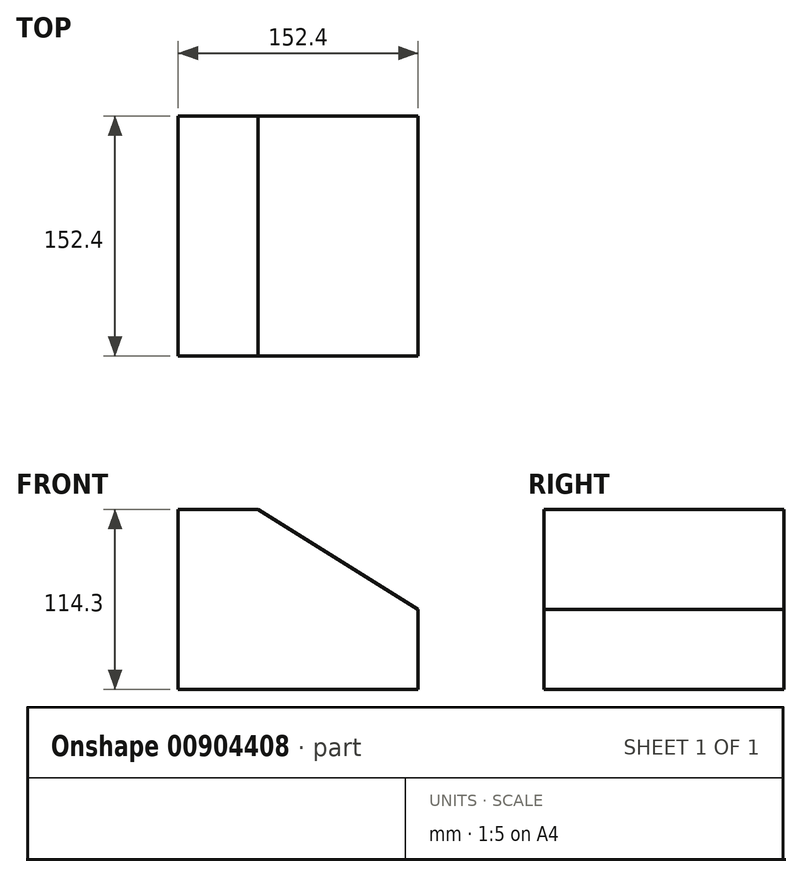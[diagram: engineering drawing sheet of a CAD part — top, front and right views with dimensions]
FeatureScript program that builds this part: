
annotation { "Feature Type Name" : "Feature", "Feature Type Description" : "" }
export const myFeature = defineFeature(function(context is Context, id is Id, definition is map)
    precondition{}
    {
        {
            var Q0;
            Q0=qCreatedBy(makeId("Front.planeOp"),FACE);
            var sketch = newSketch(context, id + "F0", { "sketchPlane" : qUnion([Q0])});
            skLineSegment(sketch, "E0.bottom", {"start": v(-76.2, 57.15) * mm, "end": v(76.2, 57.15) * mm});
            skLineSegment(sketch, "E0.top", {"start": v(-76.2, -57.15) * mm, "end": v(76.2, -57.15) * mm});
            skLineSegment(sketch, "E0.left", {"start": v(-76.2, 57.15) * mm, "end": v(-76.2, -57.15) * mm});
            skLineSegment(sketch, "E0.right", {"start": v(76.2, 57.15) * mm, "end": v(76.2, -57.15) * mm});
            skPoint(sketch, "E0.middle", {"position": v(0, 0) * mm});
            skSolve(sketch);
        }
        {
            var Q0;
            Q0=makeQuery(id+"F0.imprint","IMPRINT",FACE,{"disambiguationData":[TD([[makeQuery(id+"F0.imprint","IMPRINT",EDGE,{"derivedFrom":sQuery(id+"F0.wireOp",EDGE,"E0.bottom")}),-1.0]])]});
            extrude(context, id + "F1", {"entities" : qUnion([Q0]), "depth" : 152.4 * mm, "offsetDistance" : 25.4 * mm});
        }
        {
            var Q0;
            Q0=makeQuery(id+"F1.opExtrude","CAP_FACE",FACE,{"disambiguationData":[OSD([sQuery(id+"F0.wireOp",EDGE,"E0.bottom"),sQuery(id+"F0.wireOp",EDGE,"E0.top"),sQuery(id+"F0.wireOp",EDGE,"E0.left"),sQuery(id+"F0.wireOp",EDGE,"E0.right")])],"isStart":false});
            var sketch = newSketch(context, id + "F2", { "sketchPlane" : qUnion([Q0])});
            skLineSegment(sketch, "E1", {"start": v(-76.2, 57.15) * mm, "end": v(-25.4, 57.15) * mm});
            skLineSegment(sketch, "E2", {"start": v(-25.4, 57.15) * mm, "end": v(76.2, -6.35) * mm});
            skLineSegment(sketch, "E3", {"start": v(76.2, -6.35) * mm, "end": v(76.2, -57.15) * mm});
            skSolve(sketch);
        }
        {
            var Q0;
            {var subQ0=sQuery(id+"F2.wireOp",EDGE,"E2");Q0=makeQuery(id+"F2.imprint","IMPRINT",FACE,{"disambiguationData":[TD([[makeQuery(id+"F2.imprint","IMPRINT",EDGE,{"derivedFrom":subQ0}),1.0]])]});}
            extrude(context, id + "F3", {"entities" : qUnion([Q0]), "operationType" : NewBodyOperationType.REMOVE, "endBound" : BoundingType.THROUGH_ALL, "oppositeDirection" : true, "depth" : 25.4 * mm, "offsetDistance" : 25.4 * mm});
        }
    });
